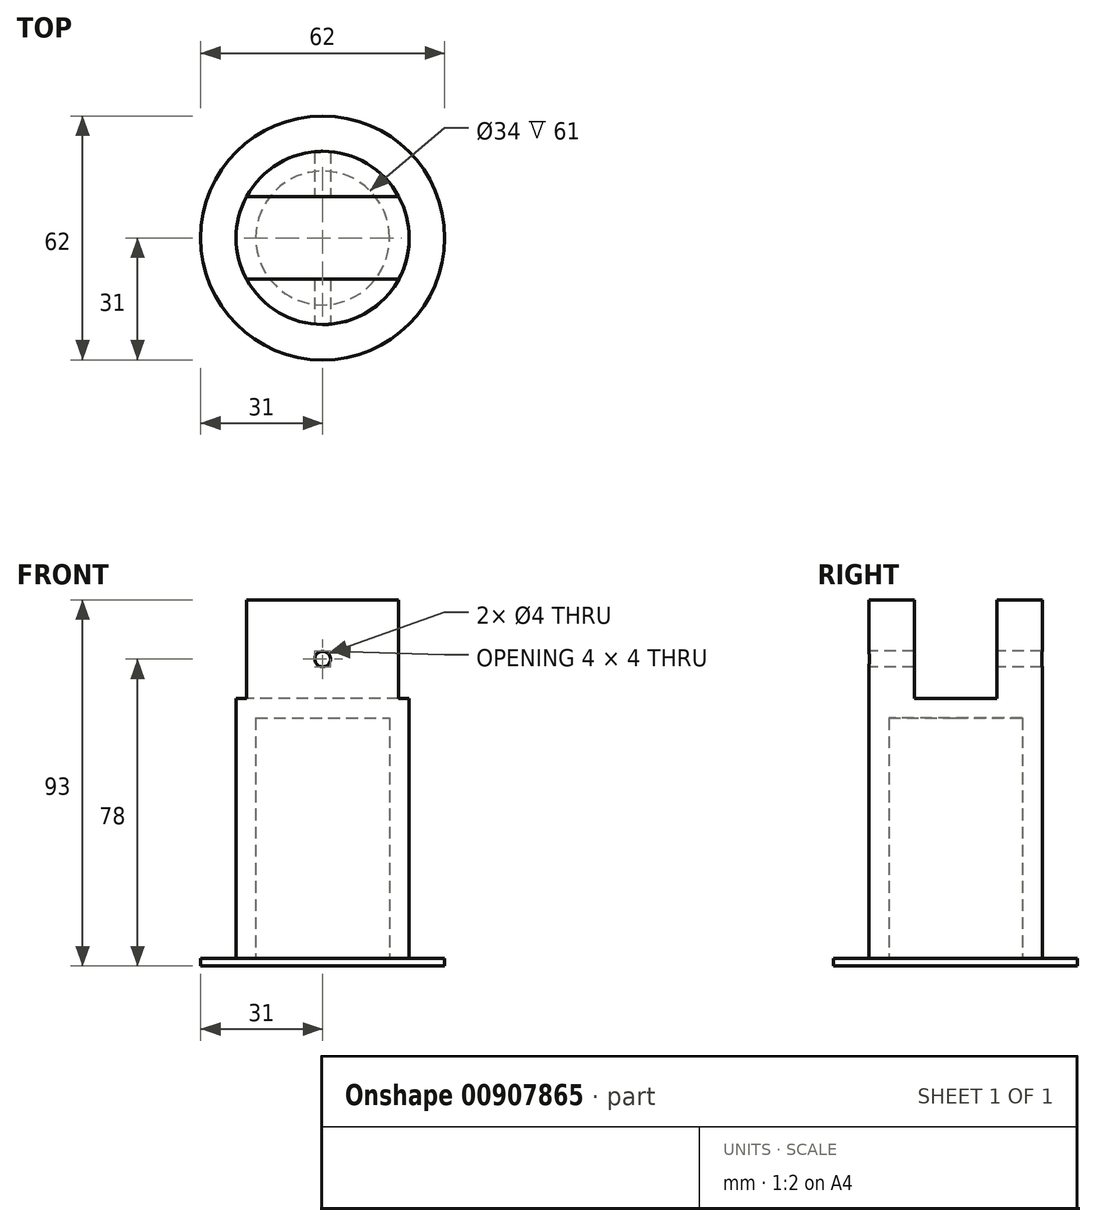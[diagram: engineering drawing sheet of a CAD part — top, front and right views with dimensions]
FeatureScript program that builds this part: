
annotation { "Feature Type Name" : "Feature", "Feature Type Description" : "" }
export const myFeature = defineFeature(function(context is Context, id is Id, definition is map)
    precondition{}
    {
        {
            var Q0;
            Q0=qCreatedBy(makeId("Top.planeOp"),FACE);
            var sketch = newSketch(context, id + "F0", { "sketchPlane" : qUnion([Q0])});
            skCircle(sketch, "E0", {"center": v(0, 0) * mm, "radius": 31 * mm});
            skSolve(sketch);
        }
        {
            var Q0;
            Q0 = qSketchRegion(id + "F0", true);
            extrude(context, id + "F1", {"entities" : qUnion([Q0]), "depth" : 2 * mm, "offsetDistance" : 25 * mm});
        }
        {
            var Q0;
            Q0=makeQuery(id+"F1.opExtrude","CAP_FACE",FACE,{"disambiguationData":[OSD([sQuery(id+"F0.wireOp",EDGE,"E0")])],"isStart":false});
            var sketch = newSketch(context, id + "F2", { "sketchPlane" : qUnion([Q0])});
            skCircle(sketch, "E1", {"center": v(0, 0) * mm, "radius": 22 * mm});
            skSolve(sketch);
        }
        {
            var Q0;
            Q0 = qSketchRegion(id + "F2", true);
            extrude(context, id + "F3", {"entities" : qUnion([Q0]), "operationType" : NewBodyOperationType.ADD, "depth" : 91 * mm, "offsetDistance" : 25 * mm});
        }
        {
            var Q0;
            Q0=makeQuery(id+"F3.opExtrude","CAP_FACE",FACE,{"disambiguationData":[OSD([sQuery(id+"F2.wireOp",EDGE,"E1")])],"isStart":false});
            var sketch = newSketch(context, id + "F4", { "sketchPlane" : qUnion([Q0])});
            skLineSegment(sketch, "E2.bottom", {"start": v(33.9, 10.5) * mm, "end": v(-33.9, 10.5) * mm});
            skLineSegment(sketch, "E2.top", {"start": v(33.9, -10.5) * mm, "end": v(-33.9, -10.5) * mm});
            skLineSegment(sketch, "E2.left", {"start": v(33.9, 10.5) * mm, "end": v(33.9, -10.5) * mm});
            skLineSegment(sketch, "E2.right", {"start": v(-33.9, 10.5) * mm, "end": v(-33.9, -10.5) * mm});
            skPoint(sketch, "E2.middle", {"position": v(0, 0) * mm});
            skSolve(sketch);
        }
        {
            var Q0;
            Q0 = qSketchRegion(id + "F4", true);
            extrude(context, id + "F5", {"entities" : qUnion([Q0]), "operationType" : NewBodyOperationType.REMOVE, "oppositeDirection" : true, "depth" : 25 * mm, "offsetDistance" : 25 * mm});
        }
        {
            var Q0;
            Q0=makeQuery(id+"F5.boolean.opBoolean","COPY",FACE,{"derivedFrom":makeQuery(id+"F5.opExtrude","SWEPT_FACE",FACE,{"disambiguationData":[OSD([sQuery(id+"F4.wireOp",EDGE,"E2.bottom")])]})});
            var sketch = newSketch(context, id + "F6", { "sketchPlane" : qUnion([Q0])});
            skLineSegment(sketch, "E3", {"start": v(19.33, 68) * mm, "end": v(-19.33, 68) * mm});
            skLineSegment(sketch, "E4", {"start": v(0, 68) * mm, "end": v(0, 93) * mm});
            skLineSegment(sketch, "E5", {"start": v(0, 68) * mm, "end": v(0, 78) * mm});
            skCircle(sketch, "E6", {"center": v(0, 78) * mm, "radius": 2 * mm});
            skSolve(sketch);
        }
        {
            var Q0;
            Q0 = qSketchRegion(id + "F6", true);
            extrude(context, id + "F7", {"entities" : qUnion([Q0]), "operationType" : NewBodyOperationType.REMOVE, "endBound" : BoundingType.THROUGH_ALL, "oppositeDirection" : true, "depth" : 25 * mm, "offsetDistance" : 25 * mm, "hasSecondDirection" : true, "secondDirectionOppositeDirection" : false, "secondDirectionDepth" : 43.7 * mm});
        }
        {
            var Q0;
            Q0=makeQuery(id+"F1.opExtrude","CAP_FACE",FACE,{"disambiguationData":[OSD([sQuery(id+"F0.wireOp",EDGE,"E0")])],"isStart":true});
            var sketch = newSketch(context, id + "F8", { "sketchPlane" : qUnion([Q0])});
            skCircle(sketch, "E7", {"center": v(0, 0) * mm, "radius": 17 * mm});
            skSolve(sketch);
        }
        {
            var Q0;
            Q0 = qSketchRegion(id + "F8", true);
            extrude(context, id + "F9", {"entities" : qUnion([Q0]), "operationType" : NewBodyOperationType.REMOVE, "oppositeDirection" : true, "depth" : 63 * mm, "offsetDistance" : 25 * mm});
        }
        {
            var Q0;
            Q0=makeQuery(id+"F1.opExtrude","CAP_FACE",FACE,{"disambiguationData":[OSD([sQuery(id+"F0.wireOp",EDGE,"E0")])],"isStart":true});
            var sketch = newSketch(context, id + "F10", { "sketchPlane" : qUnion([Q0])});
            skCircle(sketch, "E8", {"center": v(0, 0) * mm, "radius": 31 * mm});
            skSolve(sketch);
        }
        {
            var Q0;
            Q0 = qSketchRegion(id + "F10", true);
            extrude(context, id + "F11", {"entities" : qUnion([Q0]), "operationType" : NewBodyOperationType.ADD, "oppositeDirection" : true, "depth" : 2 * mm, "offsetDistance" : 25 * mm});
        }
    });
